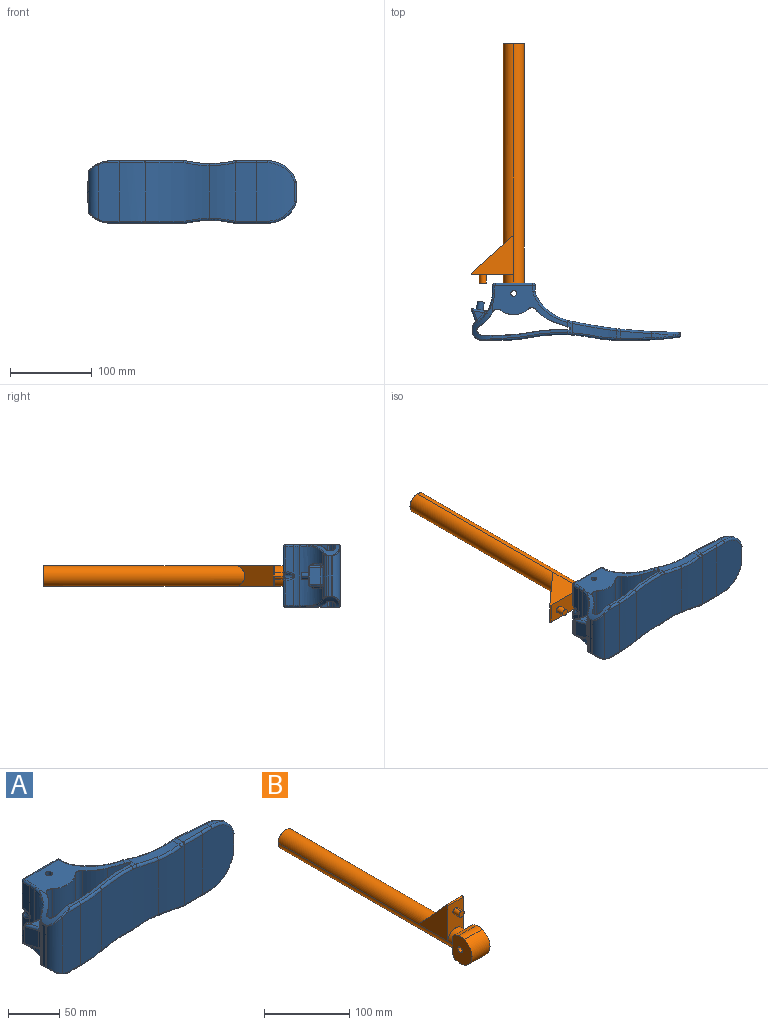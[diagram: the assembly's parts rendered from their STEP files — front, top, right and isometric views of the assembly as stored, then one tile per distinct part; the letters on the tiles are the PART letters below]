
ASSEMBLY  parts=2 mates=1
PART A: 230 faces, bbox 258.7x73.4x79.9 mm
  f0: plane 8.4x8.22mm, normal (0.17,0.98,0), area 54.5mm2, adj f11,f12
  f1: cylinder r=3.17mm len=10.25mm, axis (-0.36,-0.93,0), area 49.9mm2, adj f9,f15,f16,f18
  f2: bspline ~6.1x5.49mm, area 13.2mm2, adj f6,f7,f23,f24
  f3: bspline ~6.1x5.54mm, area 13.2mm2, adj f4,f5,f24,f25
  f4: cylinder r=36.83mm len=35.47mm, axis (0,1,0), area 128.2mm2, adj f3,f5,f25,f29,f31
  f5: bspline ~6.66x4mm, area 8.3mm2, adj f3,f4,f30,f31
  f6: cylinder r=36.83mm len=35.47mm, axis (0,1,0), area 128.8mm2, adj f2,f7,f23,f28,f36
  f7: bspline ~6.52x3.96mm, area 8.3mm2, adj f2,f6,f30,f36
  f8: sphere r=3.3mm, area 9.7mm2, adj f9,f18,f38
  f9: bspline ~11.34x4.79mm, area 26.7mm2, adj f1,f8,f15,f39
  f10: cylinder r=0.51mm len=20.32mm, axis (0,0,1), area 21.3mm2, adj f13,f14,f41,f45
  f11: cylinder r=4.17mm len=11.45mm, axis (0.17,0.98,0), area 133mm2, adj f0,f12,f45
  f12: cylinder r=4.17mm len=11.45mm, axis (0.17,0.98,0), area 133mm2, adj f0,f11,f45
  f13: bspline ~3.92x3.17mm, area 3mm2, adj f10,f46,f48
  f14: bspline ~3.59x3.55mm, area 3mm2, adj f10,f43,f49
  f15: bspline ~4.88x3.09mm, area 8.6mm2, adj f1,f9,f16,f52
  f16: bspline ~11.44x4.81mm, area 26.7mm2, adj f1,f15,f17,f53
  f17: sphere r=3.3mm, area 10.7mm2, adj f16,f18,f54
  f18: bspline ~12.36x8.25mm, area 47.7mm2, adj f1,f8,f17,f21,f55
  f19: cylinder r=2.54mm len=71.12mm, axis (0,0,1), area 283.8mm2, adj f37,f55,f56,f57
  f20: plane 33.02x12.7mm, normal (-1,0,0), area 419.4mm2, adj f22,f40,f55,f60
  f21: plane 35.62x15.3mm, normal (1,0,0), area 418.7mm2, adj f18,f22,f40,f55,f60
  f22: cylinder r=19.69mm len=39.37mm, axis (0,0,1), area 2042mm2, adj f20,f21,f40,f60
  f23: bspline ~35.21x26.69mm, area 172.4mm2, adj f2,f6,f27,f65
  f24: cylinder r=3.01mm len=24.64mm, axis (0,0,1), area 230.6mm2, adj f2,f3,f30,f65
  f25: bspline ~35.21x26.69mm, area 172.4mm2, adj f3,f4,f26,f65
  f26: torus R=302.26mm, axis (0,0,1), area 53.7mm2, adj f25,f29,f64,f65
  f27: torus R=302.26mm, axis (0,0,1), area 53.7mm2, adj f23,f28,f65,f66
  f28: plane 37.8x8.49mm, normal (0,0,-1), area 251.8mm2, adj f6,f27,f35,f63,f66
  f29: plane 37.8x8.49mm, normal (0,0,1), area 251.8mm2, adj f4,f26,f32,f64,f69
  f30: cylinder r=1.27mm len=28.33mm, axis (0,0,-1), area 6.1mm2, adj f5,f7,f24,f71
  f31: bspline ~35.98x29.26mm, area 169.7mm2, adj f4,f5,f32,f71
  f32: torus R=621.71mm, axis (0,0,1), area 150.9mm2, adj f29,f31,f33,f71
  f33: bspline ~5.75x3.16mm, area 21mm2, adj f32,f69,f70,f71
  f34: bspline ~5.7x3.16mm, area 21mm2, adj f35,f62,f63,f71
  f35: torus R=621.71mm, axis (0,0,1), area 150.9mm2, adj f28,f34,f36,f71
  f36: bspline ~35.87x28.83mm, area 169.7mm2, adj f6,f7,f35,f71
  f37: sphere r=2.54mm, area 7.6mm2, adj f19,f82,f83
  f38: cylinder r=3.3mm len=29.64mm, axis (0,0,1), area 153.7mm2, adj f8,f39,f55,f84
  f39: plane 33.43x9.7mm, normal (-1,0,0), area 290.6mm2, adj f9,f38,f52,f85
  f40: plane 39.38x32.45mm, normal (0,0,-1), area 1071.7mm2, adj f20,f21,f22,f55,f87,f88
  f41: plane 20.32x14.52mm, normal (-0.95,-0.31,0), area 310.8mm2, adj f10,f48,f49,f93
  f42: plane 11.82x10.15mm, normal (0,0,1), area 60.3mm2, adj f43,f49,f94
  f43: cylinder r=2.54mm len=17.68mm, axis (-0.98,0.17,0), area 58.9mm2, adj f14,f42,f45,f95
  f44: cylinder r=2.54mm len=12.7mm, axis (0,0,-1), area 40.7mm2, adj f45,f97,f98,f99
  f45: plane 20.32x17.24mm, normal (0.17,0.98,0), area 300.5mm2, adj f10,f11,f12,f43,f44,f46,f96,f100
  f46: cylinder r=2.54mm len=17.68mm, axis (0.98,-0.17,0), area 58.9mm2, adj f13,f45,f47,f101
  f47: plane 11.83x10.16mm, normal (0,0,-1), area 60.3mm2, adj f46,f48,f102
  f48: cylinder r=2.54mm len=15.32mm, axis (-0.31,0.95,0), area 52.3mm2, adj f13,f41,f47,f91,f103
  f49: cylinder r=2.54mm len=15.32mm, axis (0.31,-0.95,0), area 52.3mm2, adj f14,f41,f42,f92,f105
  f50: cylinder r=44.45mm len=75.72mm, axis (0,0,1), area 1913.9mm2, adj f51,f72,f77,f106
  f51: cylinder r=6.35mm len=75.72mm, axis (0,0,1), area 795.4mm2, adj f50,f61,f76,f107
  f52: cylinder r=24.77mm len=71.12mm, axis (0,0,1), area 499.1mm2, adj f15,f39,f53,f86,f104,f111
  f53: plane 33.75x10.02mm, normal (-1,0,0), area 290.6mm2, adj f16,f52,f54,f112
  f54: cylinder r=3.3mm len=29.64mm, axis (0,0,1), area 153.7mm2, adj f17,f53,f55,f113
  f55: plane 71.23x46.34mm, normal (0,1,0), area 1957.6mm2, adj f18,f19,f20,f21,f38,f40,f54,f60
  f56: plane 71.12x7.24mm, normal (1,0,0), area 514.9mm2, adj f19,f58,f82,f115
  f57: sphere r=2.54mm, area 7.6mm2, adj f19,f114,f115
  f58: cylinder r=12.7mm len=71.12mm, axis (0,0,1), area 435.2mm2, adj f56,f59,f81,f116
  f59: cylinder r=58.78mm len=71.12mm, axis (0,0,-1), area 3573mm2, adj f58,f71,f80,f117
  f60: plane 39.38x32.45mm, normal (0,0,1), area 1071.7mm2, adj f20,f21,f22,f55,f120,f121
  f61: cylinder r=26.04mm len=75.72mm, axis (0,0,1), area 2773.2mm2, adj f51,f75,f108,f123
  f62: bspline ~55.65x11.71mm, area 218.5mm2, adj f34,f71,f128,f129
  f63: cylinder r=25.4mm len=9.05mm, axis (0,1,0), area 47.4mm2, adj f28,f34,f67,f129,f133
  f64: cylinder r=2.54mm len=24.44mm, axis (-1,0,0), area 97.5mm2, adj f26,f29,f68,f134
  f65: cylinder r=304.8mm len=71.12mm, axis (0,0,1), area 2527.6mm2, adj f23,f24,f25,f26,f27,f134
  f66: cylinder r=2.54mm len=24.44mm, axis (-1,0,0), area 97.5mm2, adj f27,f28,f67,f134
  f67: bspline ~2.56x2.55mm, area 4.1mm2, adj f63,f66,f133,f134
  f68: bspline ~2.56x2.55mm, area 4.1mm2, adj f64,f69,f134,f135
  f69: cylinder r=25.4mm len=9.05mm, axis (0,-1,0), area 47.4mm2, adj f29,f33,f68,f135,f138
  f70: bspline ~55.1x11.64mm, area 218.5mm2, adj f33,f71,f138,f139
  f71: cylinder r=619.17mm len=134.12mm, axis (0,0,1), area 8960.4mm2, adj f30,f31,f32,f33,f34,f35,f36,f59
  f72: plane 75.83x20.95mm, normal (-0.33,-0.94,0), area 1671.9mm2, adj f50,f73,f78,f119,f126,f127,f140
  f73: cylinder r=1.27mm len=75.63mm, axis (0,0,1), area 268mm2, adj f72,f126,f141,f143
  f74: torus R=6.58mm, axis (0,0,1), area 4mm2, adj f75,f123,f124,f145
  f75: torus R=25.81mm, axis (0,0,1), area 13.1mm2, adj f61,f74,f76,f145
  f76: torus R=6.58mm, axis (0,0,1), area 3.8mm2, adj f51,f75,f77,f145
  f77: torus R=44.22mm, axis (0,0,1), area 9.1mm2, adj f50,f76,f78,f145
  f78: cylinder r=0.23mm len=18.77mm, axis (-0.94,0.33,0), area 7.1mm2, adj f72,f77,f140,f145
  f79: torus R=621.71mm, axis (0,0,1), area 2.8mm2, adj f71,f80,f139,f145
  f80: torus R=61.32mm, axis (0,0,-1), area 203.6mm2, adj f59,f79,f81,f145
  f81: torus R=15.24mm, axis (0,0,1), area 26.2mm2, adj f58,f80,f82,f145
  f82: cylinder r=2.54mm len=7.24mm, axis (0,1,0), area 28.9mm2, adj f37,f56,f81,f145
  f83: cylinder r=2.54mm len=46.23mm, axis (-1,0,0), area 184.4mm2, adj f37,f55,f84,f145
  f84: revolved ~3.3x3.3mm, area 14.9mm2, adj f38,f83,f85,f145
  f85: cylinder r=2.54mm len=9.4mm, axis (0,-1,0), area 37.5mm2, adj f39,f84,f86,f145
  f86: torus R=27.3mm, axis (0,0,1), area 29.3mm2, adj f52,f85,f89,f145
  f87: cylinder r=3.43mm len=21.59mm, axis (0,0,1), area 232.6mm2, adj f40,f88,f145
  f88: cylinder r=3.43mm len=21.59mm, axis (0,0,1), area 232.6mm2, adj f40,f87,f145
  f89: torus R=3.81mm, axis (0,0,1), area 3mm2, adj f86,f104,f145,f146
  f90: cylinder r=1.27mm len=60.9mm, axis (0,0,-1), area 27.5mm2, adj f148,f151,f152,f153
  f91: bspline ~4.97x3.71mm, area 9.1mm2, adj f48,f93,f103,f157
  f92: bspline ~5x3.76mm, area 9.1mm2, adj f49,f93,f105,f157
  f93: cylinder r=2.54mm len=20.32mm, axis (0,0,1), area 63.7mm2, adj f41,f91,f92,f157
  f94: torus R=35.56mm, axis (0,0,1), area 49mm2, adj f42,f95,f105,f158
  f95: bspline ~6.9x6.66mm, area 22.8mm2, adj f43,f94,f96,f158
  f96: cylinder r=2.54mm len=3.81mm, axis (0,0,-1), area 12.1mm2, adj f45,f95,f97,f158
  f97: plane 3.68x3.36mm, normal (0,0,1), area 0.2mm2, adj f44,f96,f98,f158
  f98: plane 12.7x1.98mm, normal (-0.88,0.47,0), area 28.4mm2, adj f44,f97,f99,f158
  f99: plane 3.68x3.36mm, normal (0,0,-1), area 0.2mm2, adj f44,f98,f100,f158
  f100: cylinder r=2.54mm len=3.81mm, axis (0,0,-1), area 12.1mm2, adj f45,f99,f101,f158
  f101: bspline ~6.9x6.66mm, area 22.8mm2, adj f46,f100,f102,f158
  f102: torus R=35.56mm, axis (0,0,1), area 49mm2, adj f47,f101,f103,f158
  f103: bspline ~4.68x4.48mm, area 11.9mm2, adj f48,f91,f102,f158
  f104: cylinder r=6.35mm len=71.12mm, axis (0,0,1), area 61.6mm2, adj f52,f89,f110,f158
  f105: bspline ~4.27x3.65mm, area 11.9mm2, adj f49,f92,f94,f158
  f106: torus R=44.2mm, axis (0,0,1), area 10.1mm2, adj f50,f107,f119,f160
  f107: torus R=6.6mm, axis (0,0,1), area 4.3mm2, adj f51,f106,f108,f160
  f108: torus R=25.78mm, axis (0,0,1), area 14.6mm2, adj f61,f107,f109,f160
  f109: torus R=6.6mm, axis (0,0,1), area 4.5mm2, adj f108,f122,f123,f160
  f110: torus R=3.81mm, axis (0,0,1), area 3mm2, adj f104,f111,f159,f160
  f111: torus R=27.3mm, axis (0,0,1), area 29.3mm2, adj f52,f110,f112,f160
  f112: cylinder r=2.54mm len=9.4mm, axis (0,1,0), area 37.5mm2, adj f53,f111,f113,f160
  f113: revolved ~3.3x3.3mm, area 14.9mm2, adj f54,f112,f114,f160
  f114: cylinder r=2.54mm len=46.23mm, axis (1,0,0), area 184.4mm2, adj f55,f57,f113,f160
  f115: cylinder r=2.54mm len=7.24mm, axis (0,1,0), area 28.9mm2, adj f56,f57,f116,f160
  f116: torus R=15.24mm, axis (0,0,1), area 26.2mm2, adj f58,f115,f117,f160
  f117: torus R=61.32mm, axis (0,0,-1), area 203.6mm2, adj f59,f116,f118,f160
  f118: torus R=621.71mm, axis (0,0,1), area 2.8mm2, adj f71,f117,f128,f160
  f119: cylinder r=0.25mm len=18.77mm, axis (0.94,-0.33,0), area 7.9mm2, adj f72,f106,f127,f160
  f120: cylinder r=3.43mm len=21.59mm, axis (0,0,1), area 232.6mm2, adj f60,f121,f160
  f121: cylinder r=3.43mm len=21.59mm, axis (0,0,1), area 232.6mm2, adj f60,f120,f160
  f122: torus R=44.2mm, axis (0,0,1), area 0.2mm2, adj f109,f160,f161,f162
  f123: cylinder r=6.35mm len=75.72mm, axis (0,0,1), area 841.6mm2, adj f61,f74,f109,f162
  f124: torus R=44.22mm, axis (0,0,1), area 0.2mm2, adj f74,f145,f150,f162
  f125: cylinder r=1.27mm len=60.9mm, axis (0,0,-1), area 27.5mm2, adj f149,f151,f164,f165
  f126: bspline ~3.14x1.71mm, area 1.6mm2, adj f72,f73,f127,f130,f169
  f127: bspline ~4.56x1.81mm, area 0.9mm2, adj f72,f119,f126,f169
  f128: bspline ~5.64x3.64mm, area 20.8mm2, adj f62,f71,f118,f169
  f129: cylinder r=127mm len=53.68mm, axis (0,1,0), area 565mm2, adj f62,f63,f132,f137,f169
  f130: bspline ~1.52x0.32mm, area 0.6mm2, adj f126,f143,f168,f169
  f131: bspline ~27.04x6.03mm, area 106.2mm2, adj f136,f138,f171,f213
  f132: bspline ~28.89x5.64mm, area 113.6mm2, adj f129,f133,f137,f172
  f133: bspline ~4.5x3.08mm, area 16.8mm2, adj f63,f67,f132,f172
  f134: plane 71.12x25.4mm, normal (0,-1,0), area 1806.4mm2, adj f64,f65,f66,f67,f68,f172
  f135: bspline ~4.5x3.04mm, area 16.8mm2, adj f68,f69,f136,f172
  f136: bspline ~28.89x5.64mm, area 113.6mm2, adj f131,f135,f138,f172
  f137: bspline ~27.3x6mm, area 106.2mm2, adj f129,f132,f173,f213
  f138: cylinder r=127mm len=53.68mm, axis (0,1,0), area 565mm2, adj f69,f70,f131,f136,f176
  f139: bspline ~5.64x3.64mm, area 20.8mm2, adj f70,f71,f79,f176
  f140: bspline ~2.24x0.97mm, area 0.8mm2, adj f72,f78,f141,f176
  f141: bspline ~3.07x1.6mm, area 1.4mm2, adj f73,f140,f142,f176
  f142: bspline ~1.52x0.29mm, area 0.5mm2, adj f141,f143,f176,f177
  f143: cylinder r=209.55mm len=75.72mm, axis (0,0,1), area 3807.2mm2, adj f73,f130,f142,f144,f168,f177
  f144: cylinder r=158.75mm len=75.72mm, axis (0,0,1), area 2328.4mm2, adj f143,f154,f167,f178
  f145: plane 92.09x50.96mm, normal (0,0,1), area 1852.2mm2, adj f74,f75,f76,f77,f78,f79,f80,f81
  f146: torus R=40.64mm, axis (0,0,1), area 41.3mm2, adj f89,f145,f158,f181
  f147: torus R=1.04mm, axis (0,-1,0), area 0mm2, adj f154,f179,f187,f188
  f148: bspline ~0.5x0.45mm, area 0.1mm2, adj f90,f189,f190
  f149: bspline ~0.5x0.45mm, area 0.1mm2, adj f125,f190,f191
  f150: bspline ~0.35x0.34mm, area 0.1mm2, adj f124,f162,f180,f193
  f151: plane 60.76x3.54mm, normal (1,0,0), area 215mm2, adj f90,f125,f190,f196
  f152: cylinder r=6.35mm len=68.49mm, axis (0,0,1), area 499.2mm2, adj f90,f154,f189,f197
  f153: bspline ~0.5x0.49mm, area 0.1mm2, adj f90,f196,f197
  f154: plane 75.73x25.42mm, normal (0,1,0), area 1888mm2, adj f144,f147,f152,f166,f170,f179,f188,f198
  f155: cylinder r=5.08mm len=49.28mm, axis (0,0,-1), area 72.3mm2, adj f156,f185,f195,f201
  f156: cylinder r=12.7mm len=51.35mm, axis (0,0,1), area 137.4mm2, adj f155,f157,f184,f202
  f157: cylinder r=6.35mm len=55.33mm, axis (0,0,-1), area 169.8mm2, adj f91,f92,f93,f156,f158,f183,f203
  f158: cylinder r=38.1mm len=71.12mm, axis (0,0,1), area 1717.4mm2, adj f94,f95,f96,f97,f98,f99,f100,f101
  f159: torus R=40.64mm, axis (0,0,1), area 41.2mm2, adj f110,f158,f160,f205
  f160: plane 92.04x50.88mm, normal (0,0,-1), area 1849.5mm2, adj f106,f107,f108,f109,f110,f111,f112,f113
  f161: bspline ~0.37x0.35mm, area 0.1mm2, adj f122,f162,f206,f207
  f162: cylinder r=44.45mm len=75.72mm, axis (0,0,1), area 1879.6mm2, adj f122,f123,f124,f150,f161,f163,f193,f207
  f163: cylinder r=1.27mm len=62.15mm, axis (0,0,1), area 49.9mm2, adj f162,f164,f192,f208
  f164: cylinder r=6.35mm len=61.21mm, axis (0,0,1), area 30.8mm2, adj f125,f163,f191,f209
  f165: bspline ~0.5x0.49mm, area 0.1mm2, adj f125,f196,f209
  f166: torus R=1.02mm, axis (0,1,0), area 0.1mm2, adj f154,f170,f198,f210
  f167: torus R=159mm, axis (0,0,1), area 12.3mm2, adj f144,f168,f170,f211
  f168: torus R=209.3mm, axis (0,0,1), area 19.4mm2, adj f130,f143,f167,f211
  f169: cylinder r=25.4mm len=12.6mm, axis (0,-1,0), area 55.6mm2, adj f126,f127,f128,f129,f130,f160,f173,f211
  f170: cylinder r=0.25mm len=12.95mm, axis (-1,0,0), area 5.2mm2, adj f154,f166,f167,f211
  f171: bspline ~5.52x3.1mm, area 20.8mm2, adj f131,f175,f176,f213
  f172: cylinder r=165.09mm len=71.08mm, axis (0,0,1), area 2211.1mm2, adj f132,f133,f134,f135,f136,f213
  f173: bspline ~5.52x3.1mm, area 20.8mm2, adj f137,f169,f174,f213
  f174: torus R=205.74mm, axis (0,0,1), area 190.1mm2, adj f173,f211,f212,f213
  f175: torus R=205.74mm, axis (0,0,1), area 190.1mm2, adj f171,f213,f214,f215
  f176: cylinder r=25.4mm len=12.6mm, axis (0,1,0), area 55.8mm2, adj f138,f139,f140,f141,f142,f145,f171,f215
  f177: torus R=209.32mm, axis (0,0,1), area 17.5mm2, adj f142,f143,f178,f215
  f178: torus R=158.98mm, axis (0,0,1), area 11.1mm2, adj f144,f177,f179,f215
  f179: cylinder r=0.23mm len=12.95mm, axis (-1,0,0), area 4.6mm2, adj f147,f154,f178,f215
  f180: cylinder r=1.27mm len=9.54mm, axis (0,-1,0), area 1.4mm2, adj f145,f150,f181,f217
  f181: bspline ~11.79x8.55mm, area 11.3mm2, adj f146,f180,f182,f217
  f182: bspline ~14.71x13.59mm, area 33.8mm2, adj f158,f181,f183,f217
  f183: bspline ~3.38x3.19mm, area 5.3mm2, adj f157,f182,f184,f217
  f184: bspline ~6.8x3mm, area 3mm2, adj f156,f183,f185,f217
  f185: bspline ~2.36x1.23mm, area 1.2mm2, adj f155,f184,f186,f217
  f186: cylinder r=1.27mm len=4.36mm, axis (0,1,0), area 4mm2, adj f185,f194,f195,f217
  f187: cylinder r=1.27mm len=3.58mm, axis (0,-1,0), area 0.5mm2, adj f147,f215,f216,f217
  f188: torus R=37.87mm, axis (0,1,0), area 4.7mm2, adj f147,f154,f189,f217
  f189: bspline ~6.91x5.85mm, area 3.8mm2, adj f148,f152,f188,f217
  f190: cylinder r=0.23mm len=4.04mm, axis (0,-1,0), area 1.9mm2, adj f148,f149,f151,f217
  f191: bspline ~3.13x1.56mm, area 0.3mm2, adj f149,f164,f192,f217
  f192: bspline ~1.19x1.19mm, area 0.4mm2, adj f163,f191,f193,f217
  f193: bspline ~21.88x19.8mm, area 10.9mm2, adj f150,f162,f192,f217
  f194: bspline ~2.36x1.23mm, area 1.2mm2, adj f186,f217,f218,f219
  f195: plane 48.92x4.36mm, normal (-1,0,0), area 213.1mm2, adj f155,f186,f200,f219
  f196: cylinder r=0.25mm len=4.05mm, axis (0,1,0), area 2.1mm2, adj f151,f153,f165,f221
  f197: bspline ~7.03x6.89mm, area 4.2mm2, adj f152,f153,f198,f221
  f198: torus R=37.85mm, axis (0,1,0), area 5.2mm2, adj f154,f166,f197,f221
  f199: bspline ~2.36x1.23mm, area 1.2mm2, adj f200,f219,f220,f221
  f200: cylinder r=1.27mm len=4.36mm, axis (0,-1,0), area 4mm2, adj f195,f199,f201,f221
  f201: bspline ~2.36x1.23mm, area 1.2mm2, adj f155,f200,f202,f221
  f202: bspline ~6.33x3mm, area 3mm2, adj f156,f201,f203,f221
  f203: bspline ~3.37x3.17mm, area 5.3mm2, adj f157,f202,f204,f221
  f204: bspline ~14.91x13.67mm, area 33.8mm2, adj f158,f203,f205,f221
  f205: bspline ~12.15x8.6mm, area 11.3mm2, adj f159,f204,f206,f221
  f206: cylinder r=1.27mm len=9.48mm, axis (0,1,0), area 1.4mm2, adj f160,f161,f205,f221
  f207: bspline ~25.61x23.59mm, area 12.1mm2, adj f161,f162,f208,f221
  f208: bspline ~1.23x1.22mm, area 0.5mm2, adj f163,f207,f209,f221
  f209: bspline ~3.01x1.41mm, area 0.4mm2, adj f164,f165,f208,f221
  f210: cylinder r=1.27mm len=3.56mm, axis (0,1,0), area 0.5mm2, adj f166,f211,f221,f222
  f211: plane 92.04x10.7mm, normal (0,0,-1), area 328.8mm2, adj f167,f168,f169,f170,f174,f210,f212,f223
  f212: torus R=162.56mm, axis (0,0,1), area 126.9mm2, adj f174,f211,f223,f224
  f213: cylinder r=203.2mm len=78.23mm, axis (0,0,1), area 5491.4mm2, adj f131,f137,f171,f172,f173,f174,f175,f224
  f214: torus R=162.56mm, axis (0,0,1), area 126.9mm2, adj f175,f215,f224,f225
  f215: plane 92.04x10.73mm, normal (0,0,1), area 331.2mm2, adj f175,f176,f177,f178,f179,f187,f214,f225
  f216: bspline ~7.94x3.04mm, area 8mm2, adj f187,f217,f225,f226
  f217: cylinder r=38.1mm len=42.35mm, axis (0,1,0), area 366.3mm2, adj f180,f181,f182,f183,f184,f185,f186,f187
  f218: bspline ~13.3x12.37mm, area 27mm2, adj f194,f217,f226,f227
  f219: cylinder r=5.08mm len=49.28mm, axis (0,0,1), area 72.3mm2, adj f194,f195,f199,f227
  f220: bspline ~13.3x12.92mm, area 26.8mm2, adj f199,f221,f227,f228
  f221: cylinder r=38.1mm len=42.35mm, axis (0,1,0), area 364.5mm2, adj f196,f197,f198,f199,f200,f201,f202,f203
  f222: bspline ~7.94x3.06mm, area 8mm2, adj f210,f221,f223,f228
  f223: cylinder r=2.54mm len=19.2mm, axis (-1,0,0), area 62.3mm2, adj f211,f212,f222,f229
  f224: cylinder r=165.1mm len=71.12mm, axis (0,0,1), area 2274.5mm2, adj f212,f213,f214,f229
  f225: cylinder r=2.54mm len=19.2mm, axis (-1,0,0), area 62.3mm2, adj f214,f215,f216,f229
  f226: torus R=36.83mm, axis (0,1,0), area 13.6mm2, adj f216,f217,f218,f229
  f227: cylinder r=12.7mm len=66.2mm, axis (0,0,1), area 939.2mm2, adj f218,f219,f220,f229
  f228: torus R=36.83mm, axis (0,1,0), area 13.6mm2, adj f220,f221,f222,f229
  f229: plane 71.12x25.4mm, normal (0,-1,0), area 1792.5mm2, adj f223,f224,f225,f226,f227,f228
PART B: 32 faces, bbox 29.9x324.4x71.3 mm
  f0: plane 8.43x8.4mm, normal (0,-1,0), area 55.2mm2, adj f8,f9
  f1: cylinder r=16mm len=29.85mm, axis (-1,0,0), area 297.2mm2, adj f2,f6,f10,f11
  f2: cylinder r=19.56mm len=37.31mm, axis (1,0,0), area 1485mm2, adj f1,f3,f10,f11
  f3: cylinder r=16mm len=29.85mm, axis (1,0,0), area 196.6mm2, adj f2,f7,f10,f11
  f4: cylinder r=3.81mm len=29.85mm, axis (1,0,0), area 357.2mm2, adj f5,f10,f11
  f5: cylinder r=3.81mm len=29.85mm, axis (1,0,0), area 357.2mm2, adj f4,f10,f11
  f6: plane 29.85x5.98mm, normal (0,0.26,0.97), area 184.9mm2, adj f1,f10,f11,f12
  f7: plane 29.85x6.93mm, normal (0,0.17,-0.98), area 210mm2, adj f3,f10,f11,f13
  f8: cylinder r=4.19mm len=10.16mm, axis (0,-1,0), area 133.8mm2, adj f0,f9,f15
  f9: cylinder r=4.19mm len=10.16mm, axis (0,-1,0), area 133.8mm2, adj f0,f8,f15
  f10: plane 38.96x32.34mm, normal (1,0,0), area 999.6mm2, adj f1,f2,f3,f4,f5,f6,f7,f12
  f11: plane 38.96x32.34mm, normal (-1,0,0), area 999.6mm2, adj f1,f2,f3,f4,f5,f6,f7,f12
  f12: plane 29.85x4.48mm, normal (0,0.76,0.65), area 175.9mm2, adj f6,f10,f11,f19,f20
  f13: plane 29.85x5.29mm, normal (0,0.81,-0.59), area 195mm2, adj f7,f10,f11,f19,f20
  f14: cylinder r=1.11mm len=25.4mm, axis (1,0,0), area 67.8mm2, adj f15,f17,f18,f22
  f15: plane 50.65x25.41mm, normal (0,-1,0), area 977.8mm2, adj f8,f9,f14,f18,f21,f22
  f16: plane 12.71x6.39mm, normal (0,-1,0), area 63.3mm2, adj f23,f25
  f17: plane 51.39x46.34mm, normal (0,0.74,0.67), area 1416.3mm2, adj f14,f18,f22,f27
  f18: plane 51.78x48.28mm, normal (1,0,0), area 1290.1mm2, adj f14,f15,f17,f28
  f19: plane 25.41x14.92mm, normal (0,1,0), area 125.7mm2, adj f10,f12,f13,f21,f28
  f20: plane 25.41x14.92mm, normal (0,1,0), area 125.7mm2, adj f11,f12,f13,f21,f28
  f21: cylinder r=12.7mm len=25.4mm, axis (0,1,0), area 405.4mm2, adj f15,f19,f20,f28
  f22: plane 51.78x48.28mm, normal (-1,0,0), area 1290.1mm2, adj f14,f15,f17,f28
  f23: plane 48.27x12.7mm, normal (0,0,-1), area 613mm2, adj f16,f26,f29
  f24: plane 12.78x12.71mm, normal (0,1,0), area 126.7mm2, adj f25,f29
  f25: cylinder r=6.35mm len=12.7mm, axis (0,1,0), area 202.7mm2, adj f16,f24,f29
  f26: plane 12.7x6.4mm, normal (0,0.74,0.67), area 85.3mm2, adj f23,f30
  f27: cylinder r=12.7mm len=245.13mm, axis (0,1,0), area 9614mm2, adj f17,f28,f31
  f28: cylinder r=12.7mm len=292.1mm, axis (0,1,0), area 11654.3mm2, adj f18,f19,f20,f21,f22,f27,f31
  f29: cylinder r=6.35mm len=292.1mm, axis (0,1,0), area 5827.1mm2, adj f23,f24,f25,f30,f31
  f30: cylinder r=6.35mm len=239.4mm, axis (0,1,0), area 4734.3mm2, adj f26,f29,f31
  f31: plane 25.44x25.4mm, normal (0,1,0), area 380mm2, adj f27,f28,f29,f30
PLACE A t=(-47.53,10.84,-17.88)mm fixed
PLACE B rot(axis=(0,-1,0),90deg) t=(-130.08,4.49,20.22)mm
MATE fastened B.f2 <-> A.f22  axis (0,0,1) through (-130.08,4.49,20.22)mm
